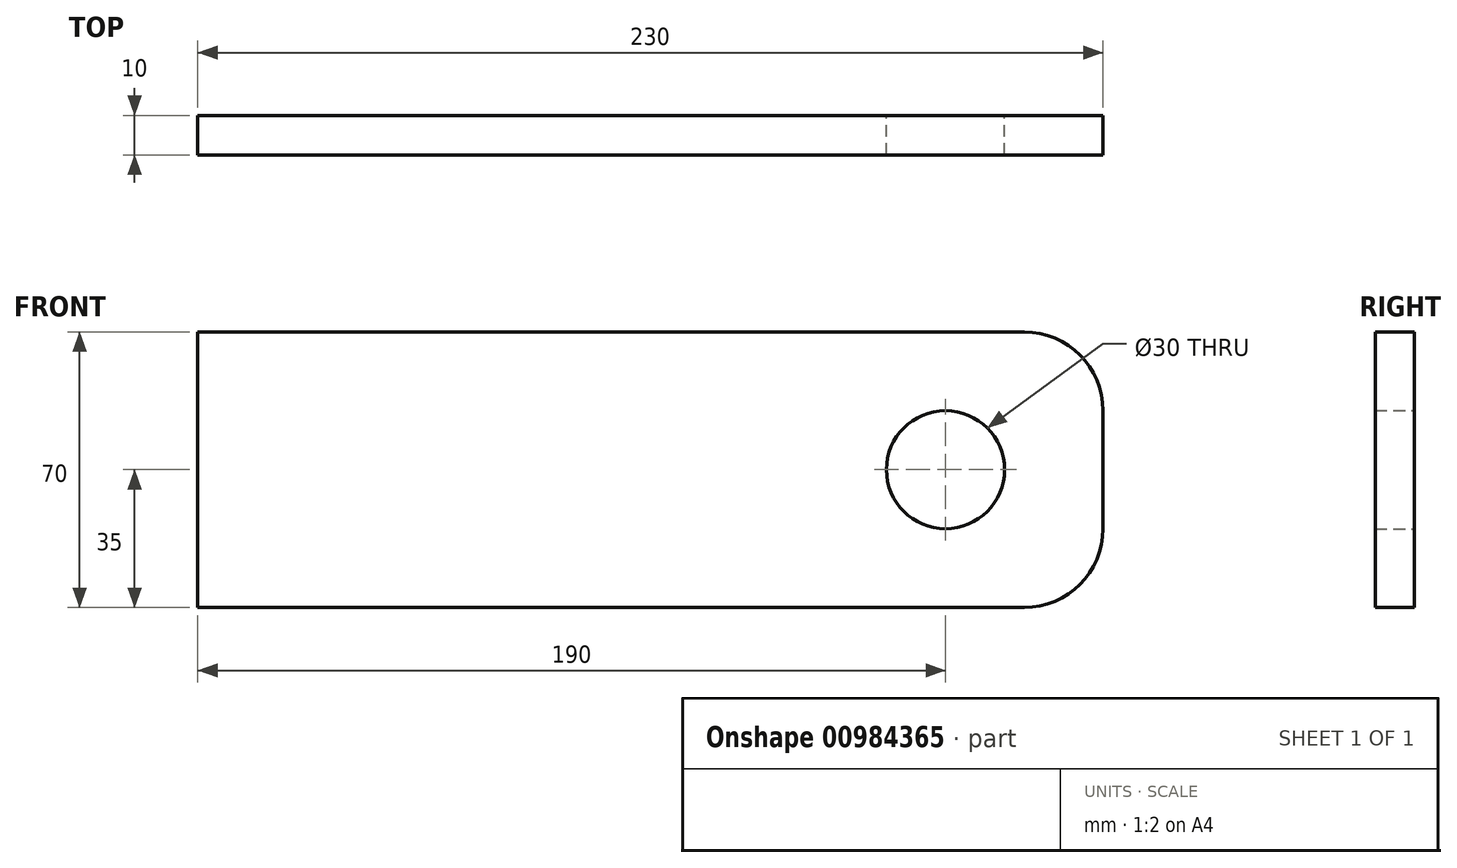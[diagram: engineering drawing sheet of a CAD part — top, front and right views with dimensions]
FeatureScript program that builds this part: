
annotation { "Feature Type Name" : "Feature", "Feature Type Description" : "" }
export const myFeature = defineFeature(function(context is Context, id is Id, definition is map)
    precondition{}
    {
        {
            var Q0;
            Q0=qCreatedBy(makeId("Front.planeOp"),FACE);
            var sketch = newSketch(context, id + "F0", { "sketchPlane" : qUnion([Q0])});
            skLineSegment(sketch, "E0.bottom", {"start": v(115, -35) * mm, "end": v(-115, -35) * mm});
            skLineSegment(sketch, "E0.top", {"start": v(115, 35) * mm, "end": v(-115, 35) * mm});
            skLineSegment(sketch, "E0.left", {"start": v(115, -35) * mm, "end": v(115, 35) * mm});
            skLineSegment(sketch, "E0.right", {"start": v(-115, -35) * mm, "end": v(-115, 35) * mm});
            skPoint(sketch, "E0.middle", {"position": v(0, 0) * mm});
            skCircle(sketch, "E1", {"center": v(75, 0) * mm, "radius": 15 * mm});
            skSolve(sketch);
        }
        {
            var Q0;
            Q0=qSketchRegion(id+"F0",true);
            extrude(context, id + "F1", {"entities" : qUnion([Q0]), "depth" : 10 * mm, "offsetDistance" : 25 * mm});
        }
        {
            var Q0;
            Q0=makeQuery(id+"F1.opExtrude","SWEPT_EDGE",EDGE,{"disambiguationData":[OSD([sQuery(id+"F0.wireOp",EDGE,"E0.top"),sQuery(id+"F0.wireOp",EDGE,"E0.left")])]});
            var Q1;
            Q1=makeQuery(id+"F1.opExtrude","SWEPT_EDGE",EDGE,{"disambiguationData":[OSD([sQuery(id+"F0.wireOp",EDGE,"E0.bottom"),sQuery(id+"F0.wireOp",EDGE,"E0.left")])]});
            fillet(context, id + "F2", {"entities" : qUnion([Q0, Q1]), "radius" : 20 * mm, "tangentPropagation" : true, "allowEdgeOverflow" : false});
        }
    });
